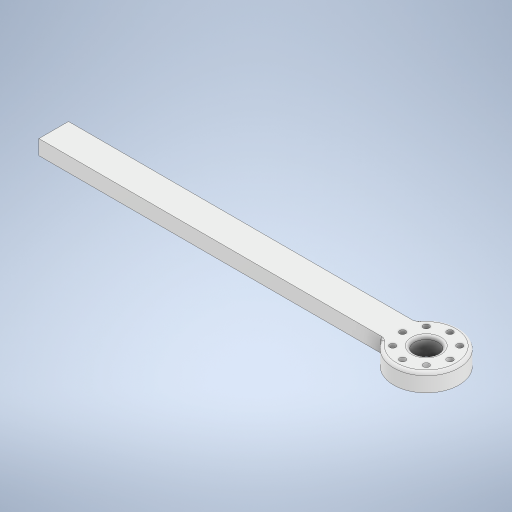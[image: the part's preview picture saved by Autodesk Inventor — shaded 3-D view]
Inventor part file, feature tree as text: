
AUTODESK INVENTOR PART (.ipt)
format: ipt  version: 2024.3 (Build 283343000, 343)  size: 319,488 bytes
history: native  units: mm
features: extrude x3, sketch x3, other x2, fillet x1
ambient origin geometry x8: Origin, YZ Plane, XZ Plane, XY Plane, X Axis, Y Axis, Z Axis, Center Point
bodies: Body1 (feature_tree)
feature tree (9):
  other  "솔리드1"
  extrude  "돌출1"  Depth=80.0mm TaperAngle=360.0deg
  fillet  "모깎기1"  Radius=115.0mm
  extrude  "돌출3"  Depth=5.0mm
  other  "두껍게 하기1"
  extrude  "돌출4"  Depth=5.0mm
  sketch  "스케치1"
  sketch  "스케치3"
  sketch  "스케치4"
